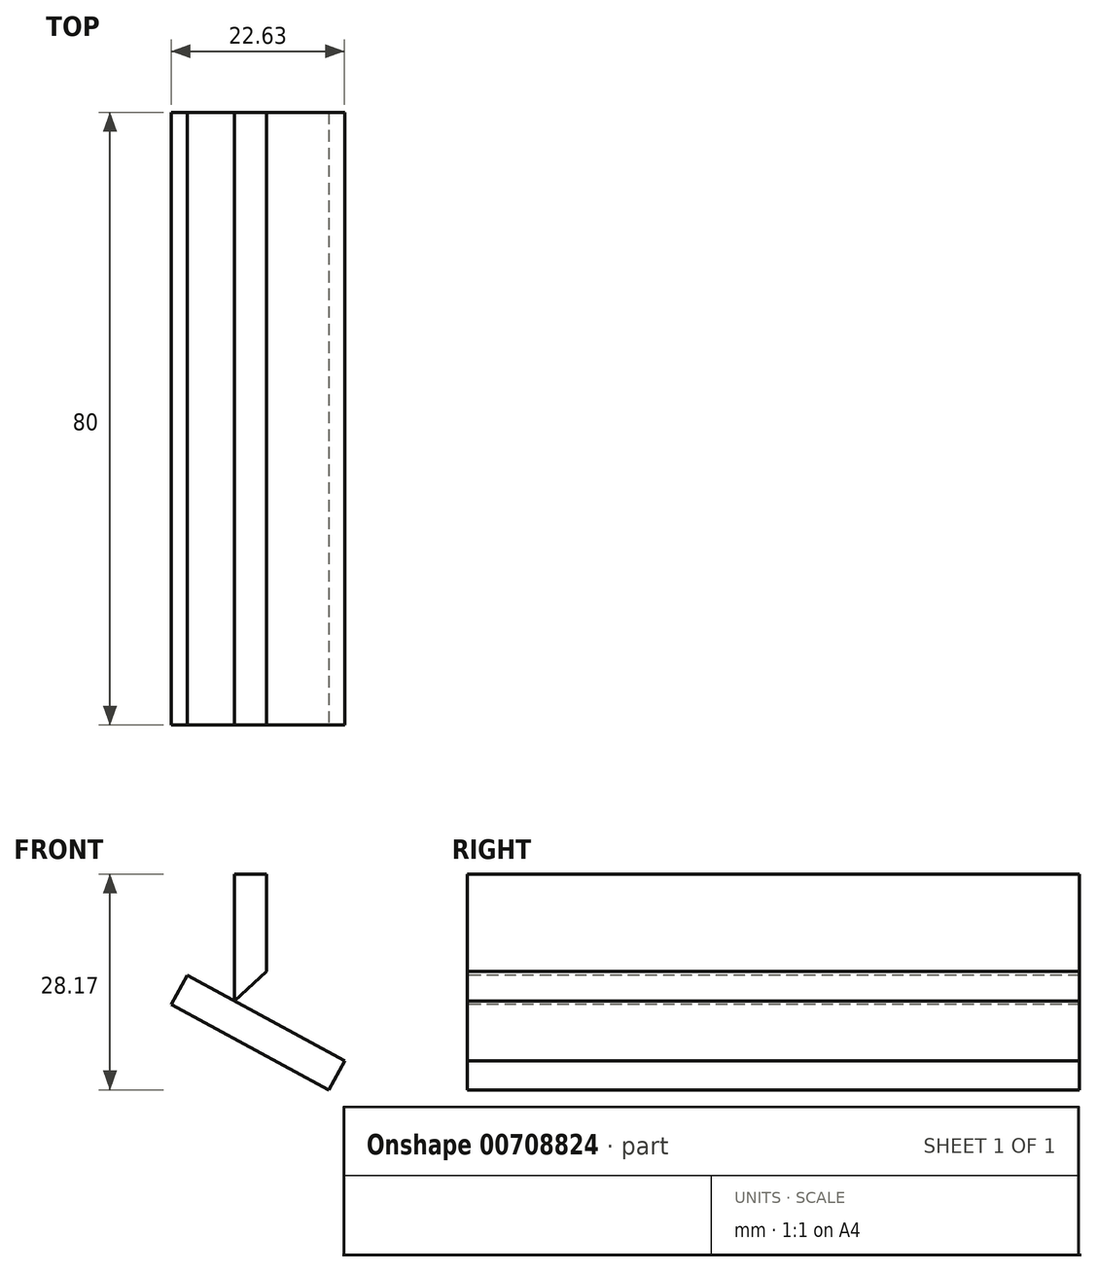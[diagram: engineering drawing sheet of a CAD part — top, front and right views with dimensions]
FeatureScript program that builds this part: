
annotation { "Feature Type Name" : "Feature", "Feature Type Description" : "" }
export const myFeature = defineFeature(function(context is Context, id is Id, definition is map)
    precondition{}
    {
        {
            var Q0;
            Q0=qCreatedBy(makeId("Front.planeOp"),FACE);
            var sketch = newSketch(context, id + "F0", { "sketchPlane" : qUnion([Q0])});
            skLineSegment(sketch, "E0", {"start": v(0, 0) * mm, "end": v(0, -16.55) * mm});
            skLineSegment(sketch, "E1", {"start": v(0, -16.55) * mm, "end": v(4.16, -12.7) * mm});
            skLineSegment(sketch, "E2", {"start": v(4.16, -12.7) * mm, "end": v(4.16, 0) * mm});
            skLineSegment(sketch, "E3", {"start": v(4.16, 0) * mm, "end": v(0, 0) * mm});
            skLineSegment(sketch, "E4", {"start": v(-6.19, -13.18) * mm, "end": v(14.37, -24.35) * mm});
            skLineSegment(sketch, "E5", {"start": v(14.37, -24.35) * mm, "end": v(12.3, -28.17) * mm});
            skLineSegment(sketch, "E6", {"start": v(12.3, -28.17) * mm, "end": v(-8.26, -17) * mm});
            skLineSegment(sketch, "E7", {"start": v(-8.26, -17) * mm, "end": v(-6.19, -13.18) * mm});
            skSolve(sketch);
        }
        {
            var Q0;
            {var subQ0=sQuery(id+"F0.wireOp",EDGE,"E5");Q0=makeQuery(id+"F0.imprint","IMPRINT",FACE,{"disambiguationData":[TD([[makeQuery(id+"F0.imprint","IMPRINT",EDGE,{"derivedFrom":subQ0}),-1.0]])]});}
            var Q1;
            Q1=makeQuery(id+"F0.imprint","IMPRINT",FACE,{"disambiguationData":[TD([[makeQuery(id+"F0.imprint","IMPRINT",EDGE,{"derivedFrom":sQuery(id+"F0.wireOp",EDGE,"E0")}),1.0]])]});
            extrude(context, id + "F1", {"entities" : qUnion([Q0, Q1]), "oppositeDirection" : true, "depth" : 80 * mm, "offsetDistance" : 25 * mm});
        }
    });
